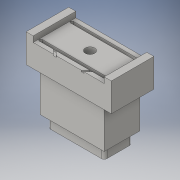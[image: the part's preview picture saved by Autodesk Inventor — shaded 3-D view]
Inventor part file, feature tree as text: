
AUTODESK INVENTOR PART (.ipt)
format: ipt  version: 2016 (Build 200138000, 138)  size: 242,176 bytes
history: native  units: mm
features: sketch x8, extrude x6, projected_geometry x6, hole x2, fillet x2
ambient origin geometry x8: Origin, YZ Plane, XZ Plane, XY Plane, X Axis, Y Axis, Z Axis, Center Point
bodies: Solid1 (feature_tree)
feature tree (24):
  extrude  "Extrusion1"  Depth=30.0mm
  extrude  "Extrusion2"  Depth=14.0mm TaperAngle=0.0deg
  extrude  "Extrusion3"  Depth=2.0mm
  extrude  "Extrusion4"  Depth=19.8mm
  hole  "Hole1"  [1 undecoded]
  fillet  "Fillet1"  Radius=1.0mm
  hole  "Hole3"  [1 undecoded]
  extrude  "Extrusion5"  Depth=0.5mm
  fillet  "Fillet2"  Radius=0.625mm
  extrude  "Extrusion7"  Depth=0.5mm
  sketch  "Sketch1"  dims[d0=15.0mm d1=30.0mm]
  sketch  "Sketch2"  dims[d2=10.0mm d3=0.0mm d5=14.0mm d6=0.0mm]
  projected_geometry  "Projected Loop1"
  sketch  "Sketch3"  dims[d7=2.0mm d8=25.0mm]
  projected_geometry  "Projected Loop2"
  sketch  "Sketch4"  dims[d9=15.0mm d10=0.0mm d11=19.8mm]
  projected_geometry  "Projected Loop3"
  sketch  "Sketch5"  dims[d12=9.8mm d13=4.0mm d14=0.0mm]
  sketch  "Sketch7"  dims[d15=3.3mm d16=6.0mm d17=4.0mm d18=2.0mm d19=90.0deg d20=8.0mm d21=20.594885mm d22=1.0mm]
  projected_geometry  "Projected Loop6"
  sketch  "Sketch8"  dims[d32=12.5mm d33=22.5mm]
  projected_geometry  "Projected Loop7"
  sketch  "Sketch13"  dims[d34=0.625mm d35=5.5mm d36=0.625mm d37=5.5mm d38=0.625mm d39=0.625mm d40=5.5mm d41=5.5mm d42=1.0mm d43=6.0mm d44=4.0mm d45=2.0mm d46=90.0deg d47=8.0mm d48=20.594885mm d49=1.0mm d50=0.625mm d51=0.999952mm d52=0.625mm d53=1.0mm d54=0.0mm d55=2.0mm d60=0.7mm d61=5.0mm d62=1.0mm d63=0.5mm d64=0.0mm]
  projected_geometry  "Projected Loop9"
note: 2 required parameter values undecoded (feature->parameter linkage not recoverable at this tier; creation-order binding heuristic only, values carry confidence <= 0.55)
